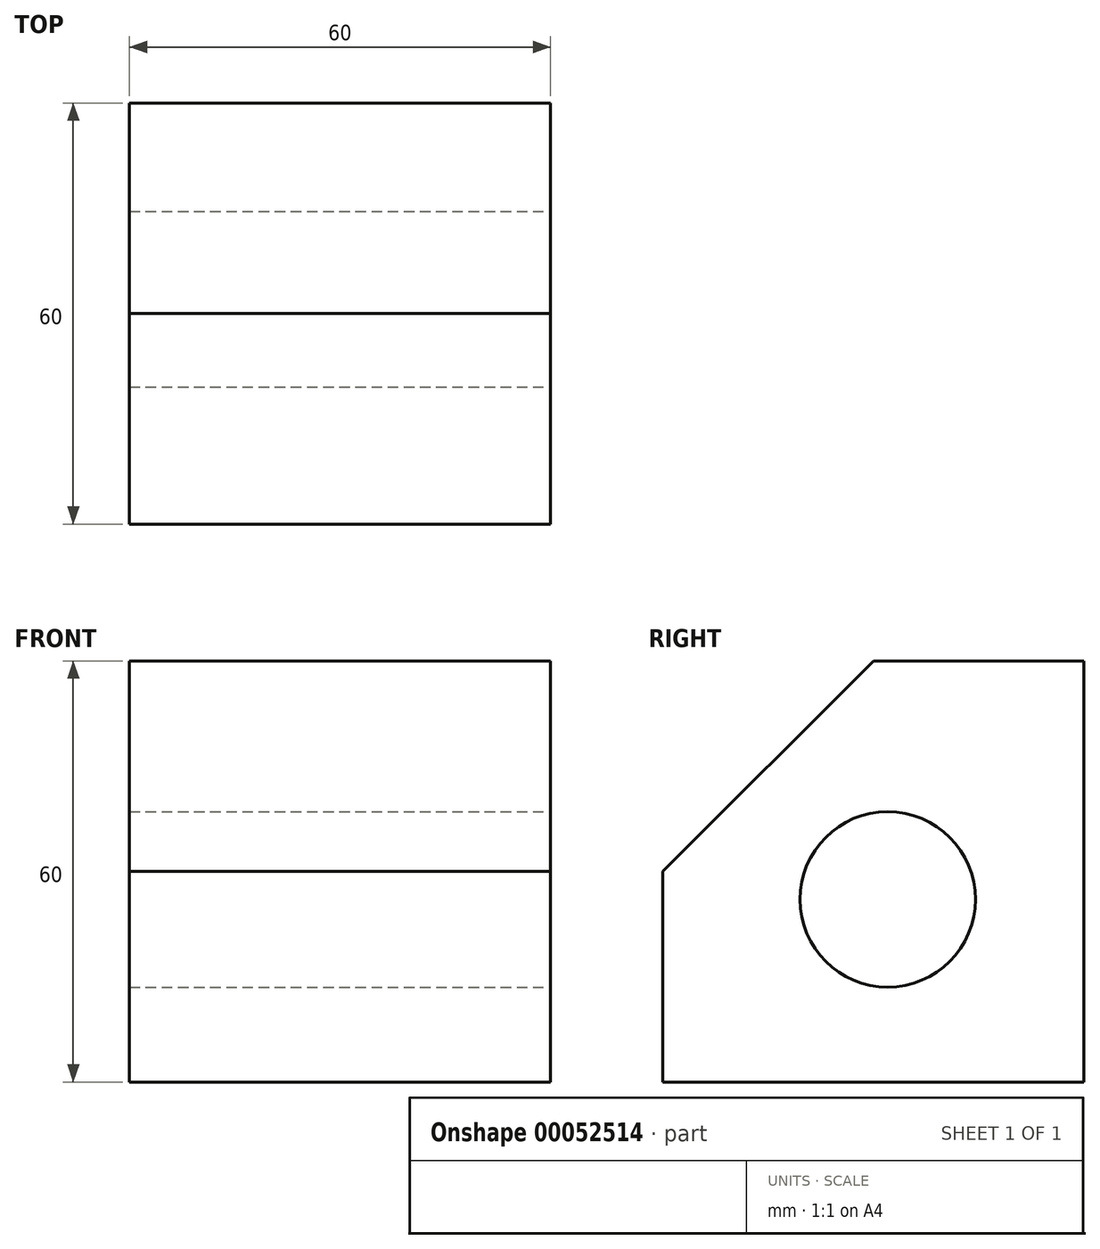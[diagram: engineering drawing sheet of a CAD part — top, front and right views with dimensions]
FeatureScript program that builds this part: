
annotation { "Feature Type Name" : "Feature", "Feature Type Description" : "" }
export const myFeature = defineFeature(function(context is Context, id is Id, definition is map)
    precondition{}
    {
        {
            var Q0;
            Q0=qCreatedBy(makeId("Right.planeOp"),FACE);
            var sketch = newSketch(context, id + "F0", { "sketchPlane" : qUnion([Q0])});
            skLineSegment(sketch, "E0", {"start": v(0, 0) * mm, "end": v(60, 0) * mm});
            skLineSegment(sketch, "E1", {"start": v(60, 0) * mm, "end": v(60, 60) * mm});
            skLineSegment(sketch, "E2", {"start": v(60, 60) * mm, "end": v(30, 60) * mm});
            skLineSegment(sketch, "E3", {"start": v(0, 0) * mm, "end": v(0, 30) * mm});
            skLineSegment(sketch, "E4", {"start": v(0, 30) * mm, "end": v(30, 60) * mm});
            skSolve(sketch);
        }
        {
            var Q0;
            Q0=makeQuery(id+"F0.imprint","IMPRINT",FACE,{"disambiguationData":[TD([[makeQuery(id+"F0.imprint","IMPRINT",EDGE,{"derivedFrom":sQuery(id+"F0.wireOp",EDGE,"E0")}),1.0]])]});
            extrude(context, id + "F1", {"entities" : qUnion([Q0]), "depth" : 60 * mm});
        }
        {
            var Q0;
            Q0=makeQuery(id+"F1.opExtrude","CAP_FACE",FACE,{"disambiguationData":[OSD([sQuery(id+"F0.wireOp",EDGE,"E0"),sQuery(id+"F0.wireOp",EDGE,"E1"),sQuery(id+"F0.wireOp",EDGE,"E2"),sQuery(id+"F0.wireOp",EDGE,"E3"),sQuery(id+"F0.wireOp",EDGE,"E4")])],"isStart":false});
            var sketch = newSketch(context, id + "F2", { "sketchPlane" : qUnion([Q0])});
            skPoint(sketch, "E5", {"position": v(32.05, 26.02) * mm});
            skSolve(sketch);
        }
        {
            var Q0;
            Q0=sQuery(id+"F2.wireOp",VERTEX,"E5");
            var Q1;
            Q1=makeQuery(id+"F1.opExtrude","SWEPT_BODY",BODY,{"disambiguationData":[OSD([sQuery(id+"F0.wireOp",EDGE,"E0"),sQuery(id+"F0.wireOp",EDGE,"E1"),sQuery(id+"F0.wireOp",EDGE,"E2"),sQuery(id+"F0.wireOp",EDGE,"E3"),sQuery(id+"F0.wireOp",EDGE,"E4")])]});
            hole(context, id + "F3", {"style" : HoleStyle.SIMPLE, "holeDiameter" : 25 * mm, "endStyle" : HoleEndStyle.THROUGH, "locations" : qUnion([Q0]), "scope" : qUnion([Q1])});
        }
    });
